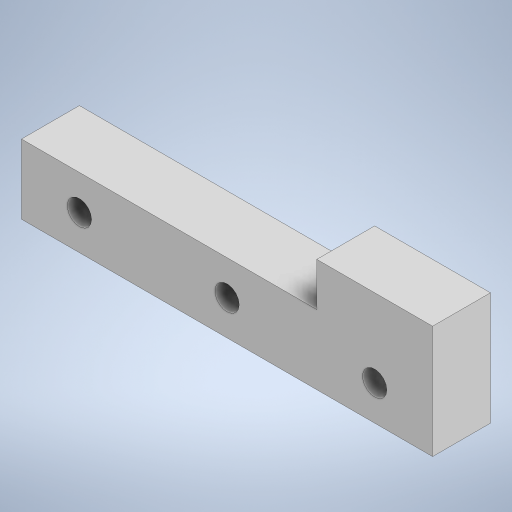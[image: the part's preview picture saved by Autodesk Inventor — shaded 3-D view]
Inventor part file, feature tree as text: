
AUTODESK INVENTOR PART (.ipt)
format: ipt  version: 2023 (Build 270158000, 158)  size: 227,840 bytes
history: native  units: in
note: dims shown in document units (in); Inventor stores cm internally (conversion verified against a paired STEP export)
features: extrude x1, sketch x1
ambient origin geometry x8: Origin, YZ Plane, XZ Plane, XY Plane, X Axis, Y Axis, Z Axis, Center Point
bodies: Solid1 (feature_tree)
feature tree (2):
  extrude  "Extrusion1"  Depth=0.4724in
  sketch  "Sketch1"  dims[d0=2.7953in d1=0.4724in d2=0.3937in d3=0.2362in d4=0.3937in d5=0.2362in d6=0.2362in d7=1.3976in d8=0.1654in d9=0.1654in d10=0.1654in d11=0.7874in d12=0.2953in d13=0.3937in d14=0.0in]
